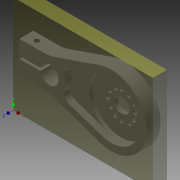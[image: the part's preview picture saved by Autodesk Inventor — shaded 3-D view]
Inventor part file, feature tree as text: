
AUTODESK INVENTOR PART (.ipt)
format: ipt  version: 2015 SP1 (Build 190203100, 203)  size: 548,352 bytes
history: native  units: in
note: dims shown in document units (in); Inventor stores cm internally (conversion verified against a paired STEP export)
features: other x6, extrude x5, sketch x4, fillet x2, hole x1, projected_geometry x1
ambient origin geometry x8: Origin, YZ Plane, XZ Plane, XY Plane, X Axis, Y Axis, Z Axis, Center Point
bodies: Solid1 (feature_tree)
feature tree (19):
  other  "Blocks"
  sketch  "Sketch1"  dims[d17=1.5748in d19=360.0deg d22=30.0deg]
  extrude  "Base"  TaperAngle=30.0deg  [1 undecoded]
  other  "BackOfBase"
  extrude  "MotorIndent"  Depth=2.0291in
  extrude  "Extrusion5"  Depth=0.75in
  fillet  "Fillet2"  Radius=0.25in
  fillet  "Fillet1"  [1 undecoded]
  extrude  "Slot"  TaperAngle=0.0deg  [1 undecoded]
  hole  "MotorCountersinks"  [1 undecoded]
  extrude  "ClampScrewHole"  Depth=0.5in
  other  "MotorMountPattern"
  sketch  "Sketch2"  dims[d23=30.0deg d24=2.0291in]
  sketch  "Sketch3"  dims[d25=0.25in d26=0.75in d27=0.25in d29=0.0in]
  sketch  "Sketch4"  dims[d30=0.35in d31=0.0in d32=1.5in d34=0.5in d35=0.35in d36=0.0in d44=-0.5in d45=0.1732in d46=0.75in d47=0.3307in d48=0.25in d49=0.5635in d50=1.0in d51=0.8108in d53=0.35in d54=0.0in d57=0.25in d58=0.225in d59=0.0in d60=0.25in]
  projected_geometry  "Projected Loop1"
  other  "MotorMountPattern:1"
  other  "MotorMountPattern:2"
  other  "MotorMountPattern:3"
note: 4 required parameter values undecoded (feature->parameter linkage not recoverable at this tier; creation-order binding heuristic only, values carry confidence <= 0.55)
